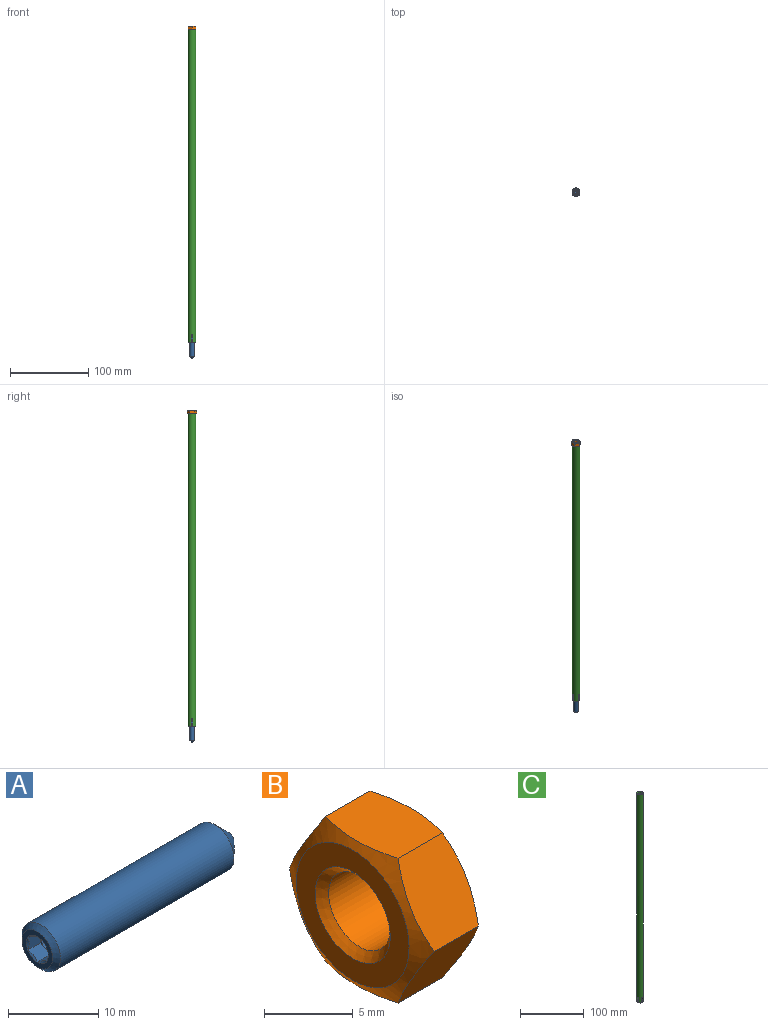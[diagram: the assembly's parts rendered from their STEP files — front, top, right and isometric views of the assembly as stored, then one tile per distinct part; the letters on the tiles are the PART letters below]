
ASSEMBLY  parts=3 mates=1
PART A: 25 faces, bbox 30x6x6 mm
  f0: cone r=1.73mm half-angle=45deg, axis (-1,0,0), area 0.4mm2, adj f10,f13
  f1: cone r=1.73mm half-angle=45deg, axis (-1,0,0), area 0.4mm2, adj f10,f14
  f2: cone r=1.73mm half-angle=45deg, axis (-1,0,0), area 0.4mm2, adj f10,f12
  f3: cone r=1.73mm half-angle=45deg, axis (-1,0,0), area 0.4mm2, adj f10,f15
  f4: cone r=1.73mm half-angle=45deg, axis (-1,0,0), area 0.4mm2, adj f10,f11
  f5: cone r=1.73mm half-angle=45deg, axis (-1,0,0), area 0.4mm2, adj f10,f16
  f6: plane 1.5x1.5mm, normal (1,0,0), area 1.8mm2, adj f7
  f7: cone r=0.75mm half-angle=45deg, axis (-1,0,0), area 37.5mm2, adj f6,f8
  f8: cylinder r=3mm len=27.14mm, axis (-1,0,0), area 511.5mm2, adj f7,f9
  f9: cone r=3mm half-angle=45deg, axis (1,0,0), area 14.7mm2, adj f8,f10
  f10: plane 4.77x4.77mm, normal (-1,0,0), area 8.5mm2, adj f0,f1,f2,f3,f4,f5,f9
  f11: plane 2x1.5mm, normal (0,-0.5,-0.87), area 3.2mm2, adj f4,f12,f16,f19,f20
  f12: plane 2x1.5mm, normal (0,0.5,-0.87), area 3.2mm2, adj f2,f11,f13,f18,f19
  f13: plane 2x1.74mm, normal (0,1,0), area 3.2mm2, adj f0,f12,f14,f17,f18
  f14: plane 2x1.5mm, normal (0,0.5,0.87), area 3.2mm2, adj f1,f13,f15,f17,f22
  f15: plane 2x1.5mm, normal (0,-0.5,0.87), area 3.2mm2, adj f3,f14,f16,f21,f22
  f16: plane 2x1.74mm, normal (0,-1,0), area 3.2mm2, adj f5,f11,f15,f20,f21
  f17: plane 1.3x0.75mm, normal (-1,0,0), area 0.1mm2, adj f13,f14,f24
  f18: plane 1.3x0.75mm, normal (-1,0,0), area 0.1mm2, adj f12,f13,f24
  f19: plane 1.5x0.43mm, normal (-1,0,0), area 0.1mm2, adj f11,f12,f24
  f20: plane 1.3x0.75mm, normal (-1,0,0), area 0.1mm2, adj f11,f16,f24
  f21: plane 1.3x0.75mm, normal (-1,0,0), area 0.1mm2, adj f15,f16,f24
  f22: plane 1.5x0.43mm, normal (-1,0,0), area 0.1mm2, adj f14,f15,f24
  f23: cone r=1.5mm half-angle=60deg, axis (-1,0,0), area 8.2mm2, adj f24
  f24: cylinder r=1.5mm len=3mm, axis (-1,0,0), area 9.4mm2, adj f17,f18,f19,f20,f21,f22,f23
PART B: 13 faces, bbox 5.5x12x12 mm
  f0: plane 9x9mm, normal (-1,0,0), area 35.3mm2, adj f1,f4
  f1: cone r=4.5mm half-angle=60deg, axis (1,0,0), area 27.4mm2, adj f0,f7,f8,f9,f10,f11,f12
  f2: cone r=6mm half-angle=60deg, axis (-1,0,0), area 26.5mm2, adj f3,f7,f8,f9,f10,f11,f12
  f3: plane 9x9mm, normal (1,0,0), area 35.3mm2, adj f2,f6
  f4: cone r=3mm half-angle=45deg, axis (-1,0,0), area 13.1mm2, adj f0,f5
  f5: cylinder r=2.46mm len=4.92mm, axis (1,0,0), area 60.5mm2, adj f4,f6
  f6: cone r=2.46mm half-angle=45deg, axis (1,0,0), area 13.1mm2, adj f3,f5
  f7: plane 5.78x4.43mm, normal (0,0,1), area 23.8mm2, adj f1,f2,f8,f12
  f8: plane 5x4.43mm, normal (0,0.87,0.5), area 23.8mm2, adj f1,f2,f7,f9
  f9: plane 5x4.43mm, normal (0,0.87,-0.5), area 23.8mm2, adj f1,f2,f8,f10
  f10: plane 6.25x4.9mm, normal (0,0,-1), area 23.8mm2, adj f1,f2,f9,f11
  f11: plane 5x4.43mm, normal (0,-0.87,-0.5), area 23.8mm2, adj f1,f2,f10,f12
  f12: plane 5x4.43mm, normal (0,-0.87,0.5), area 23.8mm2, adj f1,f2,f7,f11
PART C: 19 faces, bbox 10.2x10.2x400 mm
  f0: plane 4x4mm, normal (0,0,-1), area 8.8mm2, adj f1,f6,f12,f13
  f1: plane 10x2.07mm, normal (0,1,0), area 20.7mm2, adj f0,f3,f12,f13
  f2: plane 10x2.07mm, normal (0,-1,0), area 20.7mm2, adj f3,f12,f13,f14
  f3: plane 2.17x2mm, normal (0,0,-1), area 4mm2, adj f1,f2,f12,f13
  f4: plane 4x4mm, normal (0,0,-1), area 8.8mm2, adj f5,f10,f12,f13
  f5: plane 10x2.07mm, normal (-1,0,0), area 20.7mm2, adj f4,f7,f12,f13
  f6: plane 10x2.07mm, normal (1,0,0), area 20.7mm2, adj f0,f7,f12,f13
  f7: plane 2.17x2mm, normal (0,0,-1), area 4mm2, adj f5,f6,f12,f13
  f8: plane 4x4mm, normal (0,0,-1), area 8.8mm2, adj f9,f12,f13,f18
  f9: plane 10x2.07mm, normal (0,-1,0), area 20.7mm2, adj f8,f11,f12,f13
  f10: plane 10x2.07mm, normal (0,1,0), area 20.7mm2, adj f4,f11,f12,f13
  f11: plane 2.17x2mm, normal (0,0,-1), area 4mm2, adj f9,f10,f12,f13
  f12: cylinder r=3.1mm len=400mm, axis (0,0,-1), area 7709.7mm2, adj f0,f1,f2,f3,f4,f5,f6,f7
  f13: cylinder r=5.1mm len=400mm, axis (0,0,-1), area 12737.2mm2, adj f0,f1,f2,f3,f4,f5,f6,f7
  f14: plane 4x4mm, normal (0,0,-1), area 8.8mm2, adj f2,f12,f13,f17
  f15: plane 10.2x10.2mm, normal (0,0,1), area 51.5mm2, adj f12,f13
  f16: plane 2.17x2mm, normal (0,0,-1), area 4mm2, adj f12,f13,f17,f18
  f17: plane 10x2.07mm, normal (1,0,0), area 20.7mm2, adj f12,f13,f14,f16
  f18: plane 10x2.07mm, normal (-1,0,0), area 20.7mm2, adj f8,f12,f13,f16
PLACE A rot(axis=(-0.58,0.58,0.58),120deg) t=(0,0,10)mm
PLACE B rot(axis=(0.71,0,-0.71),180deg) t=(0,0,405)mm
PLACE C at identity
MATE fastened B.f1 <-> C.f13  axis (0,0,-1) through (0,0,400)mm
